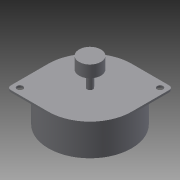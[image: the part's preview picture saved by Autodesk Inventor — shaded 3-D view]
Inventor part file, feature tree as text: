
AUTODESK INVENTOR PART (.ipt)
format: ipt  version: 2013 (Build 170138000, 138)  size: 113,664 bytes
history: native  units: mm
features: extrude x4, sketch x4, projected_geometry x2
ambient origin geometry x8: Origin, YZ Plane, XZ Plane, XY Plane, X Axis, Y Axis, Z Axis, Center Point
bodies: Solid1 (feature_tree)
feature tree (10):
  extrude  "Extrusion1"  Depth=15.0mm TaperAngle=0.0deg
  extrude  "Extrusion2"  Depth=15.0mm TaperAngle=0.0deg
  extrude  "Extrusion3"  Depth=3.0mm
  extrude  "Extrusion4"  Depth=25.0mm
  sketch  "Sketch1"  dims[d0=42.0mm d1=15.0mm d2=0.0mm]
  sketch  "Sketch2"  dims[d3=3.0mm d4=15.0mm d5=0.0mm]
  projected_geometry  "Projected Loop1"
  sketch  "Sketch3"  dims[d6=2.0mm d7=3.0mm]
  projected_geometry  "Projected Loop2"
  sketch  "Sketch4"  dims[d8=3.0mm d9=25.0mm d10=25.0mm d11=1.0mm d12=0.0mm d13=11.0mm d14=6.0mm d15=0.0mm]
